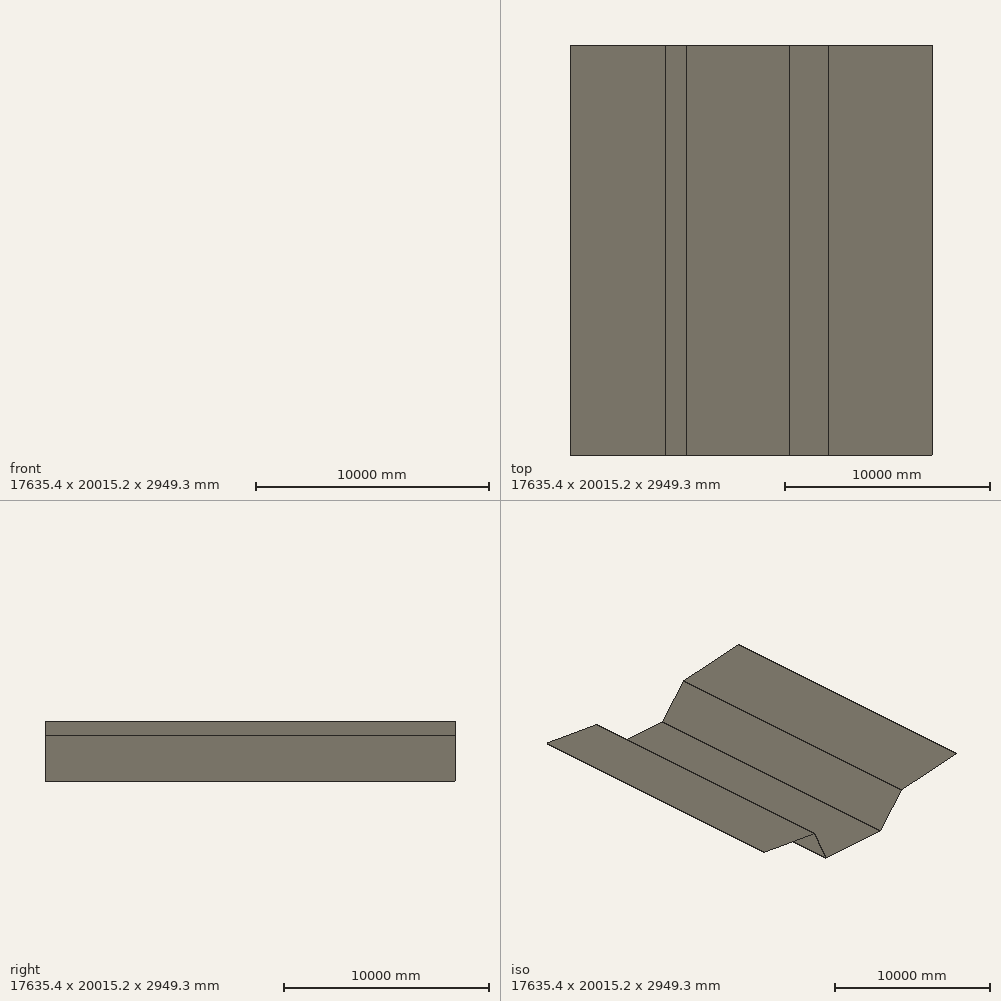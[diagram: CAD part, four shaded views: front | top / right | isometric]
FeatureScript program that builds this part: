
annotation { "Feature Type Name" : "Feature", "Feature Type Description" : "" }
export const myFeature = defineFeature(function(context is Context, id is Id, definition is map)
    precondition{}
    {
        {
            var Q0;
            Q0=qCreatedBy(makeId("Front.planeOp"),FACE);
            var sketch = newSketch(context, id + "F0", { "sketchPlane" : qUnion([Q0])});
            skLineSegment(sketch, "E0", {"start": v(-8822.52, 1292.96) * mm, "end": v(-4219.63, 816.65) * mm});
            skLineSegment(sketch, "E1", {"start": v(-4219.63, 816.65) * mm, "end": v(-3154.65, -1457.15) * mm});
            skLineSegment(sketch, "E2", {"start": v(-3154.65, -1457.15) * mm, "end": v(1845.35, -1457.15) * mm});
            skLineSegment(sketch, "E3", {"start": v(1845.35, -1457.15) * mm, "end": v(3776.76, 816.65) * mm});
            skLineSegment(sketch, "E4", {"start": v(3776.76, 816.65) * mm, "end": v(8812.86, 1492.16) * mm});
            skSolve(sketch);
        }
        {
            var Q0;
            Q0 = qSketchRegion(id + "F0", true);
            var Q1;
            Q1=sQuery(id+"F0.wireOp",EDGE,"E0");
            var Q2;
            Q2=sQuery(id+"F0.wireOp",EDGE,"E1");
            var Q3;
            Q3=sQuery(id+"F0.wireOp",EDGE,"E2");
            var Q4;
            Q4=sQuery(id+"F0.wireOp",EDGE,"E3");
            var Q5;
            Q5=sQuery(id+"F0.wireOp",EDGE,"E4");
            extrude(context, id + "F1", {"entities" : qUnion([Q0]), "bodyType" : ToolBodyType.SURFACE, "surfaceEntities" : qUnion([Q1, Q2, Q3, Q4, Q5]), "depth" : 20015.2 * mm, "offsetDistance" : 25.4 * mm});
        }
    });
